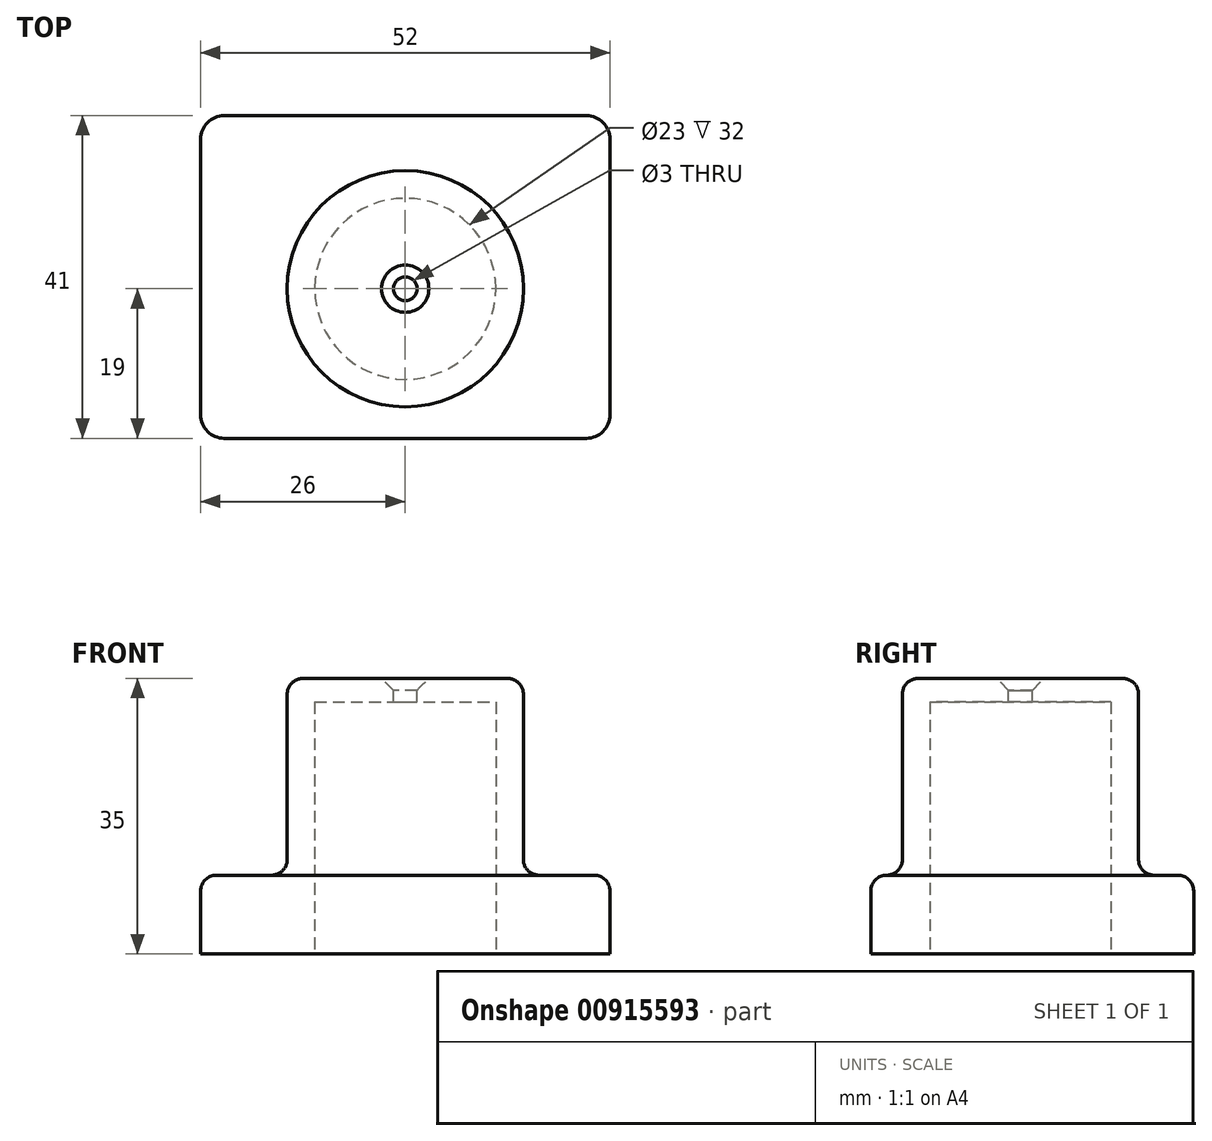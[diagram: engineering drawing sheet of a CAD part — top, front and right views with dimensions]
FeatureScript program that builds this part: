
annotation { "Feature Type Name" : "Feature", "Feature Type Description" : "" }
export const myFeature = defineFeature(function(context is Context, id is Id, definition is map)
    precondition{}
    {
        {
            var Q0;
            Q0=qCreatedBy(makeId("Top.planeOp"),FACE);
            var sketch = newSketch(context, id + "F0", { "sketchPlane" : qUnion([Q0])});
            skLineSegment(sketch, "E0.bottom", {"start": v(0, 0) * mm, "end": v(52, 0) * mm});
            skLineSegment(sketch, "E0.top", {"start": v(0, 41) * mm, "end": v(52, 41) * mm});
            skLineSegment(sketch, "E0.left", {"start": v(0, 0) * mm, "end": v(0, 41) * mm});
            skLineSegment(sketch, "E0.right", {"start": v(52, 0) * mm, "end": v(52, 41) * mm});
            skSolve(sketch);
        }
        {
            var Q0;
            Q0 = qSketchRegion(id + "F0", true);
            extrude(context, id + "F1", {"entities" : qUnion([Q0]), "depth" : 10 * mm, "offsetDistance" : 25 * mm});
        }
        {
            var Q0;
            Q0=makeQuery(id+"F1.opExtrude","CAP_FACE",FACE,{"disambiguationData":[OSD([sQuery(id+"F0.wireOp",EDGE,"E0.bottom"),sQuery(id+"F0.wireOp",EDGE,"E0.top"),sQuery(id+"F0.wireOp",EDGE,"E0.left"),sQuery(id+"F0.wireOp",EDGE,"E0.right")])],"isStart":false});
            var sketch = newSketch(context, id + "F2", { "sketchPlane" : qUnion([Q0])});
            skLineSegment(sketch, "E1", {"start": v(26, 0) * mm, "end": v(26, 19) * mm});
            skCircle(sketch, "E2", {"center": v(26, 19) * mm, "radius": 11 * mm});
            skCircle(sketch, "E3.0", {"center": v(26, 19) * mm, "radius": 15 * mm});
            skSolve(sketch);
        }
        {
            var Q0;
            Q0 = qSketchRegion(id + "F2", true);
            extrude(context, id + "F3", {"entities" : qUnion([Q0]), "operationType" : NewBodyOperationType.ADD, "depth" : 20 * mm, "offsetDistance" : 25 * mm});
        }
        {
            var Q0;
            Q0=makeQuery(id+"F3.boolean.opBoolean","SPLIT",FACE,{"disambiguationData":[TD([makeQuery(id+"F3.opExtrude","SWEPT_FACE",FACE,{"disambiguationData":[OSD([sQuery(id+"F2.wireOp",EDGE,"E2")])]})])],"derivedFrom":makeQuery(id+"F1.opExtrude","CAP_FACE",FACE,{"disambiguationData":[OSD([sQuery(id+"F0.wireOp",EDGE,"E0.bottom"),sQuery(id+"F0.wireOp",EDGE,"E0.top"),sQuery(id+"F0.wireOp",EDGE,"E0.left"),sQuery(id+"F0.wireOp",EDGE,"E0.right")])],"isStart":false})});
            var sketch = newSketch(context, id + "F4", { "sketchPlane" : qUnion([Q0])});
            skCircle(sketch, "E4", {"center": v(26, 19) * mm, "radius": 11 * mm});
            skSolve(sketch);
        }
        {
            var Q0;
            Q0 = qSketchRegion(id + "F4", true);
            extrude(context, id + "F5", {"entities" : qUnion([Q0]), "operationType" : NewBodyOperationType.REMOVE, "endBound" : BoundingType.THROUGH_ALL, "oppositeDirection" : true, "depth" : 5 * mm, "offsetDistance" : 25 * mm});
        }
        {
            var Q0;
            Q0=makeQuery(id+"F3.opExtrude","CAP_FACE",FACE,{"disambiguationData":[OSD([sQuery(id+"F2.wireOp",EDGE,"E2"),sQuery(id+"F2.wireOp",EDGE,"E3.0")])],"isStart":false});
            var sketch = newSketch(context, id + "F6", { "sketchPlane" : qUnion([Q0])});
            skCircle(sketch, "E5", {"center": v(26, 19) * mm, "radius": 15 * mm});
            skSolve(sketch);
        }
        {
            var Q0;
            Q0 = qSketchRegion(id + "F6", true);
            extrude(context, id + "F7", {"entities" : qUnion([Q0]), "operationType" : NewBodyOperationType.ADD, "depth" : 5 * mm, "offsetDistance" : 25 * mm});
        }
        {
            var Q0;
            Q0=makeQuery(id+"F7.opExtrude","CAP_EDGE",EDGE,{"disambiguationData":[OSD([sQuery(id+"F6.wireOp",EDGE,"E5")])],"isStart":false});
            fillet(context, id + "F8", {"entities" : qUnion([Q0]), "radius" : 2 * mm, "tangentPropagation" : true, "allowEdgeOverflow" : false});
        }
        {
            var Q0;
            Q0=makeQuery(id+"F1.opExtrude","SWEPT_EDGE",EDGE,{"disambiguationData":[OSD([sQuery(id+"F0.wireOp",EDGE,"E0.bottom"),sQuery(id+"F0.wireOp",EDGE,"E0.right")])]});
            var Q1;
            Q1=makeQuery(id+"F1.opExtrude","SWEPT_EDGE",EDGE,{"disambiguationData":[OSD([sQuery(id+"F0.wireOp",EDGE,"E0.bottom"),sQuery(id+"F0.wireOp",EDGE,"E0.left")])]});
            var Q2;
            Q2=makeQuery(id+"F1.opExtrude","SWEPT_EDGE",EDGE,{"disambiguationData":[OSD([sQuery(id+"F0.wireOp",EDGE,"E0.top"),sQuery(id+"F0.wireOp",EDGE,"E0.left")])]});
            var Q3;
            Q3=makeQuery(id+"F1.opExtrude","SWEPT_EDGE",EDGE,{"disambiguationData":[OSD([sQuery(id+"F0.wireOp",EDGE,"E0.top"),sQuery(id+"F0.wireOp",EDGE,"E0.right")])]});
            fillet(context, id + "F9", {"entities" : qUnion([Q0, Q1, Q2, Q3]), "radius" : 3 * mm, "tangentPropagation" : true, "allowEdgeOverflow" : false});
        }
        {
            var Q0;
            Q0=makeQuery(id+"F1.opExtrude","CAP_FACE",FACE,{"disambiguationData":[OSD([sQuery(id+"F0.wireOp",EDGE,"E0.bottom"),sQuery(id+"F0.wireOp",EDGE,"E0.top"),sQuery(id+"F0.wireOp",EDGE,"E0.left"),sQuery(id+"F0.wireOp",EDGE,"E0.right")])],"isStart":true});
            var sketch = newSketch(context, id + "F10", { "sketchPlane" : qUnion([Q0])});
            skCircle(sketch, "E6", {"center": v(26, -19) * mm, "radius": 9.5 * mm});
            skCircle(sketch, "E7", {"center": v(26, -19) * mm, "radius": 11.5 * mm});
            skSolve(sketch);
        }
        {
            var Q0;
            Q0 = qSketchRegion(id + "F10", true);
            extrude(context, id + "F11", {"entities" : qUnion([Q0]), "operationType" : NewBodyOperationType.ADD, "oppositeDirection" : true, "depth" : 35 * mm, "offsetDistance" : 25 * mm});
        }
        {
            var Q0;
            {var subQ0=sQuery(id+"F0.wireOp",EDGE,"E0.left");var subQ1=sQuery(id+"F0.wireOp",EDGE,"E0.top");var subQ2=sQuery(id+"F0.wireOp",EDGE,"E0.right");var subQ3=sQuery(id+"F0.wireOp",EDGE,"E0.bottom");Q0=makeQuery(id+"F3.boolean.opBoolean","SPLIT",FACE,{"disambiguationData":[TD([makeQuery(id+"F1.opExtrude","SWEPT_FACE",FACE,{"disambiguationData":[OSD([subQ3])]})])],"derivedFrom":makeQuery(id+"F1.opExtrude","CAP_FACE",FACE,{"disambiguationData":[OSD([subQ3,subQ1,subQ0,subQ2])],"isStart":false})});}
            fillet(context, id + "F12", {"entities" : qUnion([Q0]), "radius" : 2 * mm, "tangentPropagation" : true, "allowEdgeOverflow" : false});
        }
        {
            var Q0;
            Q0=makeQuery(id+"F11.boolean.opBoolean","MERGE",FACE,{"derivedFrom":[makeQuery(id+"F1.opExtrude","CAP_FACE",FACE,{"disambiguationData":[OSD([sQuery(id+"F0.wireOp",EDGE,"E0.bottom"),sQuery(id+"F0.wireOp",EDGE,"E0.top"),sQuery(id+"F0.wireOp",EDGE,"E0.left"),sQuery(id+"F0.wireOp",EDGE,"E0.right")])],"isStart":true}),makeQuery(id+"F11.opExtrude","CAP_FACE",FACE,{"disambiguationData":[OSD([sQuery(id+"F10.wireOp",EDGE,"E6"),sQuery(id+"F10.wireOp",EDGE,"E7")])],"isStart":true})]});
            var sketch = newSketch(context, id + "F13", { "sketchPlane" : qUnion([Q0])});
            skCircle(sketch, "E8.0", {"center": v(26, -19) * mm, "radius": 10 * mm});
            skSolve(sketch);
        }
        {
            var Q0;
            Q0 = qSketchRegion(id + "F13", true);
            extrude(context, id + "F14", {"entities" : qUnion([Q0]), "operationType" : NewBodyOperationType.REMOVE, "oppositeDirection" : true, "depth" : 32 * mm, "offsetDistance" : 25 * mm});
        }
        {
            var Q0;
            Q0=makeQuery(id+"F11.boolean.opBoolean","MERGE",FACE,{"derivedFrom":[makeQuery(id+"F1.opExtrude","CAP_FACE",FACE,{"disambiguationData":[OSD([sQuery(id+"F0.wireOp",EDGE,"E0.bottom"),sQuery(id+"F0.wireOp",EDGE,"E0.top"),sQuery(id+"F0.wireOp",EDGE,"E0.left"),sQuery(id+"F0.wireOp",EDGE,"E0.right")])],"isStart":true}),makeQuery(id+"F11.opExtrude","CAP_FACE",FACE,{"disambiguationData":[OSD([sQuery(id+"F10.wireOp",EDGE,"E6"),sQuery(id+"F10.wireOp",EDGE,"E7")])],"isStart":true})]});
            var sketch = newSketch(context, id + "F15", { "sketchPlane" : qUnion([Q0])});
            skCircle(sketch, "E9", {"center": v(26, -19) * mm, "radius": 11.5 * mm});
            skSolve(sketch);
        }
        {
            var Q0;
            Q0 = qSketchRegion(id + "F15", true);
            var Q1;
            Q1=makeQuery(id+"F14.boolean.opBoolean","COPY",FACE,{"derivedFrom":makeQuery(id+"F14.opExtrude","CAP_FACE",FACE,{"disambiguationData":[OSD([sQuery(id+"F13.wireOp",EDGE,"E8.0")])],"isStart":false})});
            extrude(context, id + "F16", {"entities" : qUnion([Q0]), "operationType" : NewBodyOperationType.REMOVE, "endBound" : BoundingType.UP_TO_SURFACE, "oppositeDirection" : true, "depth" : 9 * mm, "endBoundEntityFace" : qUnion([Q1]), "offsetDistance" : 25 * mm});
        }
        {
            var Q0;
            Q0=makeQuery(id+"F7.opExtrude","CAP_FACE",FACE,{"disambiguationData":[OSD([sQuery(id+"F6.wireOp",EDGE,"E5")])],"isStart":false});
            var sketch = newSketch(context, id + "F17", { "sketchPlane" : qUnion([Q0])});
            skCircle(sketch, "E10", {"center": v(26, 19) * mm, "radius": 1.5 * mm});
            skSolve(sketch);
        }
        {
            var Q0;
            Q0=sQuery(id+"F17.wireOp",VERTEX,"E10.center");
            var Q1;
            Q1=makeQuery(id+"F1.opExtrude","SWEPT_BODY",BODY,{"disambiguationData":[OSD([sQuery(id+"F0.wireOp",EDGE,"E0.bottom"),sQuery(id+"F0.wireOp",EDGE,"E0.top"),sQuery(id+"F0.wireOp",EDGE,"E0.left"),sQuery(id+"F0.wireOp",EDGE,"E0.right")])]});
            hole(context, id + "F18", {"style" : HoleStyle.C_SINK, "endStyle" : HoleEndStyle.THROUGH, "holeDiameter" : 3 * mm, "cSinkDiameter" : 6 * mm, "cSinkAngle" : 90 * degree, "majorDiameter" : 5 * mm, "isTappedThrough" : true, "tappedDepth" : 12 * mm, "tapClearance" : 3, "locations" : qUnion([Q0]), "scope" : qUnion([Q1])});
        }
    });
